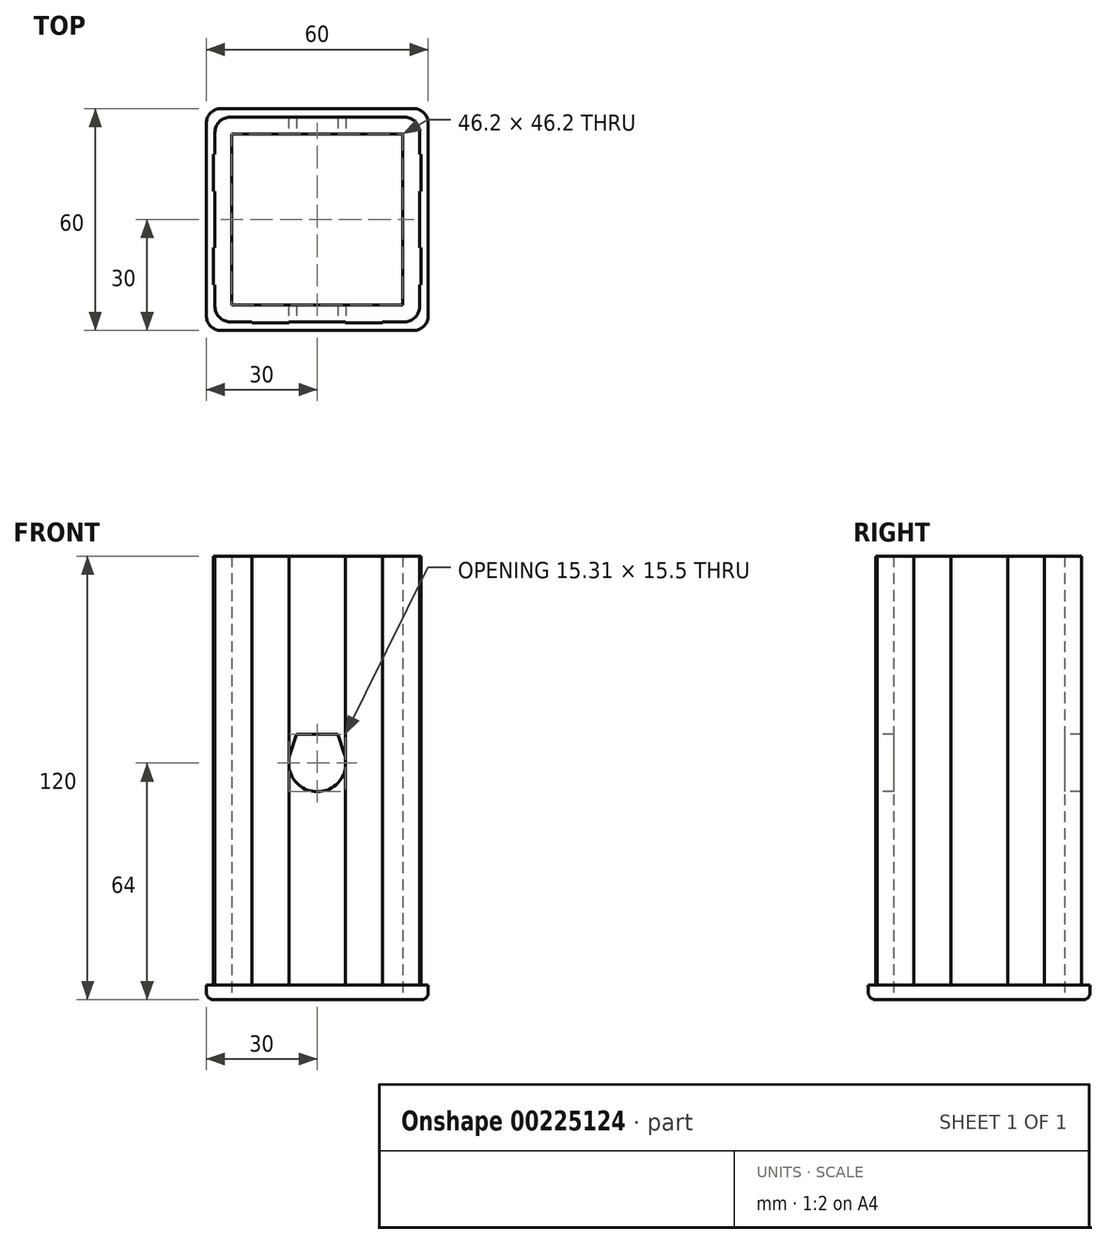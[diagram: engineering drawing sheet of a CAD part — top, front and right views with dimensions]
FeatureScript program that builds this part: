
annotation { "Feature Type Name" : "Feature", "Feature Type Description" : "" }
export const myFeature = defineFeature(function(context is Context, id is Id, definition is map)
    precondition{}
    {
        {
            var Q0;
            Q0=qCreatedBy(makeId("Top.planeOp"),FACE);
            var sketch = newSketch(context, id + "F0", { "sketchPlane" : qUnion([Q0])});
            skLineSegment(sketch, "E0.bottom", {"start": v(30, 30) * mm, "end": v(-30, 30) * mm});
            skLineSegment(sketch, "E0.top", {"start": v(30, -30) * mm, "end": v(-30, -30) * mm});
            skLineSegment(sketch, "E0.left", {"start": v(30, 30) * mm, "end": v(30, -30) * mm});
            skLineSegment(sketch, "E0.right", {"start": v(-30, 30) * mm, "end": v(-30, -30) * mm});
            skPoint(sketch, "E0.middle", {"position": v(0, 0) * mm});
            skLineSegment(sketch, "E1.bottom", {"start": v(23.1, 23.1) * mm, "end": v(-23.1, 23.1) * mm});
            skLineSegment(sketch, "E1.top", {"start": v(23.1, -23.1) * mm, "end": v(-23.1, -23.1) * mm});
            skLineSegment(sketch, "E1.left", {"start": v(23.1, 23.1) * mm, "end": v(23.1, -23.1) * mm});
            skLineSegment(sketch, "E1.right", {"start": v(-23.1, 23.1) * mm, "end": v(-23.1, -23.1) * mm});
            skLineSegment(sketch, "E2.bottom", {"start": v(27.65, 27.65) * mm, "end": v(-27.65, 27.65) * mm});
            skLineSegment(sketch, "E2.top", {"start": v(27.65, -27.65) * mm, "end": v(17.65, -27.65) * mm});
            skLineSegment(sketch, "E2.left", {"start": v(27.65, 27.65) * mm, "end": v(27.65, 17.65) * mm});
            skLineSegment(sketch, "E2.right", {"start": v(-27.65, 27.65) * mm, "end": v(-27.65, 17.65) * mm});
            skLineSegment(sketch, "E3", {"start": v(27.65, 17.65) * mm, "end": v(28.05, 17.65) * mm});
            skLineSegment(sketch, "E4", {"start": v(28.05, 17.65) * mm, "end": v(28.05, 7.65) * mm});
            skLineSegment(sketch, "E5", {"start": v(27.65, 7.65) * mm, "end": v(28.05, 7.65) * mm});
            skLineSegment(sketch, "E6.trimOffspring", {"start": v(27.65, 7.65) * mm, "end": v(27.65, -7.65) * mm});
            skLineSegment(sketch, "E7", {"start": v(27.65, -17.65) * mm, "end": v(28.05, -17.65) * mm});
            skLineSegment(sketch, "E8", {"start": v(28.05, -17.65) * mm, "end": v(28.05, -7.65) * mm});
            skLineSegment(sketch, "E9", {"start": v(28.05, -7.65) * mm, "end": v(27.65, -7.65) * mm});
            skLineSegment(sketch, "E10.trimOffspring", {"start": v(27.65, -17.65) * mm, "end": v(27.65, -27.65) * mm});
            skLineSegment(sketch, "E11", {"start": v(17.65, -27.65) * mm, "end": v(17.65, -27.95) * mm});
            skLineSegment(sketch, "E12", {"start": v(17.65, -27.95) * mm, "end": v(7.65, -27.95) * mm});
            skLineSegment(sketch, "E13", {"start": v(7.65, -27.95) * mm, "end": v(7.65, -27.65) * mm});
            skLineSegment(sketch, "E14", {"start": v(-7.65, -27.65) * mm, "end": v(-7.65, -27.95) * mm});
            skLineSegment(sketch, "E15", {"start": v(-7.65, -27.95) * mm, "end": v(-17.65, -27.95) * mm});
            skLineSegment(sketch, "E16", {"start": v(-17.65, -27.95) * mm, "end": v(-17.65, -27.65) * mm});
            skLineSegment(sketch, "E17", {"start": v(-27.65, -17.65) * mm, "end": v(-28.05, -17.65) * mm});
            skLineSegment(sketch, "E18", {"start": v(-28.05, -17.65) * mm, "end": v(-28.05, -7.65) * mm});
            skLineSegment(sketch, "E19", {"start": v(-28.05, -7.65) * mm, "end": v(-27.65, -7.65) * mm});
            skLineSegment(sketch, "E20", {"start": v(-27.65, 17.65) * mm, "end": v(-28.05, 17.65) * mm});
            skLineSegment(sketch, "E21", {"start": v(-28.05, 17.65) * mm, "end": v(-28.05, 7.65) * mm});
            skLineSegment(sketch, "E22", {"start": v(-28.05, 7.65) * mm, "end": v(-27.65, 7.65) * mm});
            skLineSegment(sketch, "E23.trimOffspring", {"start": v(-27.65, 7.65) * mm, "end": v(-27.65, -7.65) * mm});
            skLineSegment(sketch, "E24.trimOffspring", {"start": v(-27.65, -17.65) * mm, "end": v(-27.65, -27.65) * mm});
            skLineSegment(sketch, "E25.trimOffspring", {"start": v(-17.65, -27.65) * mm, "end": v(-27.65, -27.65) * mm});
            skLineSegment(sketch, "E26.trimOffspring", {"start": v(7.65, -27.65) * mm, "end": v(-7.65, -27.65) * mm});
            skSolve(sketch);
        }
        {
            var Q0;
            Q0=makeQuery(id+"F0.imprint","IMPRINT",FACE,{"disambiguationData":[TD([[makeQuery(id+"F0.imprint","IMPRINT",EDGE,{"derivedFrom":sQuery(id+"F0.wireOp",EDGE,"E1.bottom")}),-1.0]])]});
            extrude(context, id + "F1", {"entities" : qUnion([Q0]), "depth" : 116 * mm});
        }
        {
            var Q0;
            Q0=makeQuery(id+"F0.imprint","IMPRINT",FACE,{"disambiguationData":[TD([[makeQuery(id+"F0.imprint","IMPRINT",EDGE,{"derivedFrom":sQuery(id+"F0.wireOp",EDGE,"E0.bottom")}),1.0]])]});
            var Q1;
            Q1=makeQuery(id+"F0.imprint","IMPRINT",FACE,{"disambiguationData":[TD([[makeQuery(id+"F0.imprint","IMPRINT",EDGE,{"derivedFrom":sQuery(id+"F0.wireOp",EDGE,"E1.bottom")}),-1.0]])]});
            extrude(context, id + "F2", {"entities" : qUnion([Q0, Q1]), "operationType" : NewBodyOperationType.ADD, "oppositeDirection" : true, "depth" : 4 * mm});
        }
        {
            var Q0;
            Q0=makeQuery(id+"F1.opExtrude","SWEPT_EDGE",EDGE,{"disambiguationData":[OSD([sQuery(id+"F0.wireOp",EDGE,"E2.top"),sQuery(id+"F0.wireOp",EDGE,"E10.trimOffspring")])]});
            var Q1;
            Q1=makeQuery(id+"F1.opExtrude","SWEPT_EDGE",EDGE,{"disambiguationData":[OSD([sQuery(id+"F0.wireOp",EDGE,"E24.trimOffspring"),sQuery(id+"F0.wireOp",EDGE,"E25.trimOffspring")])]});
            var Q2;
            Q2=makeQuery(id+"F1.opExtrude","SWEPT_EDGE",EDGE,{"disambiguationData":[OSD([sQuery(id+"F0.wireOp",EDGE,"E2.bottom"),sQuery(id+"F0.wireOp",EDGE,"E2.left")])]});
            var Q3;
            Q3=makeQuery(id+"F1.opExtrude","SWEPT_EDGE",EDGE,{"disambiguationData":[OSD([sQuery(id+"F0.wireOp",EDGE,"E2.bottom"),sQuery(id+"F0.wireOp",EDGE,"E2.right")])]});
            var Q4;
            Q4=makeQuery(id+"F2.opExtrude","SWEPT_EDGE",EDGE,{"disambiguationData":[OSD([sQuery(id+"F0.wireOp",EDGE,"E0.bottom"),sQuery(id+"F0.wireOp",EDGE,"E0.right")])]});
            var Q5;
            Q5=makeQuery(id+"F2.opExtrude","SWEPT_EDGE",EDGE,{"disambiguationData":[OSD([sQuery(id+"F0.wireOp",EDGE,"E0.bottom"),sQuery(id+"F0.wireOp",EDGE,"E0.left")])]});
            var Q6;
            Q6=makeQuery(id+"F2.opExtrude","SWEPT_EDGE",EDGE,{"disambiguationData":[OSD([sQuery(id+"F0.wireOp",EDGE,"E0.top"),sQuery(id+"F0.wireOp",EDGE,"E0.right")])]});
            var Q7;
            Q7=makeQuery(id+"F2.opExtrude","SWEPT_EDGE",EDGE,{"disambiguationData":[OSD([sQuery(id+"F0.wireOp",EDGE,"E0.top"),sQuery(id+"F0.wireOp",EDGE,"E0.left")])]});
            fillet(context, id + "F3", {"entities" : qUnion([Q0, Q1, Q2, Q3, Q4, Q5, Q6, Q7]), "radius" : 4 * mm, "tangentPropagation" : true, "allowEdgeOverflow" : false});
        }
        {
            var Q0;
            Q0=makeQuery(id+"F2.opExtrude","CAP_EDGE",EDGE,{"disambiguationData":[OSD([sQuery(id+"F0.wireOp",EDGE,"E0.left")])],"isStart":false});
            fillet(context, id + "F4", {"entities" : qUnion([Q0]), "radius" : 2 * mm, "tangentPropagation" : true, "allowEdgeOverflow" : false});
        }
        {
            var Q0;
            Q0=qCreatedBy(makeId("Front.planeOp"),FACE);
            cPlane(context, id + "F5", {"entities" : qUnion([Q0]), "cplaneType" : CPlaneType.OFFSET, "offset" : 27.65 * mm, "width" : 150 * mm, "height" : 150 * mm});
        }
        {
            var Q0;
            Q0=qCreatedBy(id+"F5.planeOp",FACE);
            var sketch = newSketch(context, id + "F6", { "sketchPlane" : qUnion([Q0])});
            skArc(sketch, "E27", {"start": v(-7.37, 62.4) * mm, "mid": v(0, 52.25) * mm, "end": v(7.37, 62.4) * mm});
            skArc(sketch, "E28.cCircle", {"start": v(-7.37, 62.4) * mm, "mid": v(0, 52.25) * mm, "end": v(7.37, 62.4) * mm, "construction": true});
            skLineSegment(sketch, "E28.0", {"start": v(-5.63, 67.75) * mm, "end": v(5.63, 67.75) * mm});
            skLineSegment(sketch, "E28.1", {"start": v(5.63, 67.75) * mm, "end": v(7.37, 62.4) * mm});
            skLineSegment(sketch, "E28.4", {"start": v(-7.37, 62.4) * mm, "end": v(-5.63, 67.75) * mm});
            skPoint(sketch, "E28.0.midPoint", {"position": v(0, 67.75) * mm});
            skPoint(sketch, "E29.orphan", {"position": v(0, 50.42) * mm});
            skPoint(sketch, "E30.orphan", {"position": v(-9.11, 57.04) * mm});
            skSolve(sketch);
        }
        {
            var Q0;
            Q0=makeQuery(id+"F6.imprint","IMPRINT",FACE,{"disambiguationData":[TD([[makeQuery(id+"F6.imprint","IMPRINT",EDGE,{"derivedFrom":sQuery(id+"F6.wireOp",EDGE,"E27")}),1.0]])]});
            extrude(context, id + "F7", {"entities" : qUnion([Q0]), "operationType" : NewBodyOperationType.REMOVE, "oppositeDirection" : true, "depth" : 80 * mm});
        }
    });
